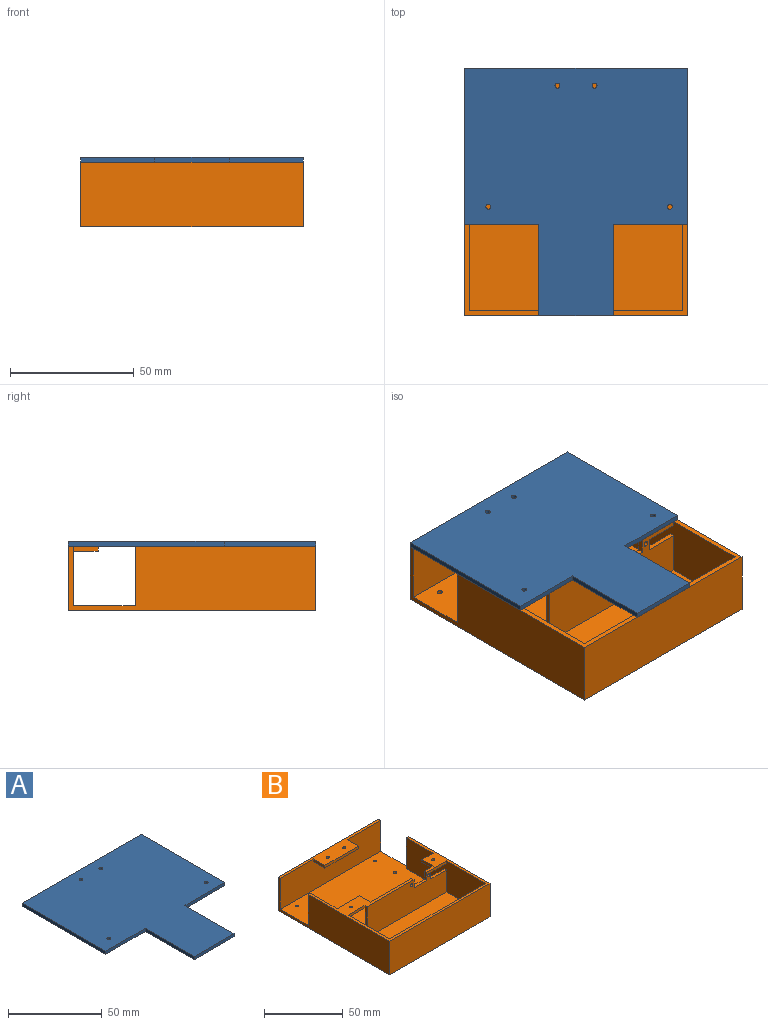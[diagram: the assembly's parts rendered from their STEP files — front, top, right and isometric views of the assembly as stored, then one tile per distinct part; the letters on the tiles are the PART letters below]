
ASSEMBLY  parts=2 mates=1
PART A: 14 faces, bbox 90x100x2 mm
  f0: plane 30x2mm, normal (0,-1,0), area 60mm2, adj f1,f10,f12,f13
  f1: plane 37x2mm, normal (-1,0,0), area 74mm2, adj f0,f2,f12,f13
  f2: plane 30x2mm, normal (0,-1,0), area 60mm2, adj f1,f3,f12,f13
  f3: plane 37x2mm, normal (1,0,0), area 74mm2, adj f2,f4,f12,f13
  f4: plane 30x2mm, normal (0,-1,0), area 60mm2, adj f3,f5,f12,f13
  f5: plane 63x2mm, normal (1,0,0), area 126mm2, adj f4,f6,f12,f13
  f6: plane 90x2mm, normal (0,1,0), area 180mm2, adj f5,f10,f12,f13
  f7: cylinder r=1mm len=2mm, axis (0,0,-1), area 12.6mm2, adj f12,f13
  f8: cylinder r=1mm len=2mm, axis (0,0,-1), area 12.6mm2, adj f12,f13
  f9: cylinder r=1mm len=2mm, axis (0,0,-1), area 12.6mm2, adj f12,f13
  f10: plane 63x2mm, normal (-1,0,0), area 126mm2, adj f0,f6,f12,f13
  f11: cylinder r=1mm len=2mm, axis (0,0,-1), area 12.6mm2, adj f12,f13
  f12: plane 100x90mm, normal (0,0,1), area 6767.4mm2, adj f0,f1,f2,f3,f4,f5,f6,f7
  f13: plane 100x90mm, normal (0,0,-1), area 6767.4mm2, adj f0,f1,f2,f3,f4,f5,f6,f7
PART B: 43 faces, bbox 90x100x26 mm
  f0: plane 71x24mm, normal (0,1,0), area 1528.9mm2, adj f1,f4,f5,f20,f22,f24,f26,f29
  f1: plane 90x73mm, normal (0,0,1), area 877.5mm2, adj f0,f2,f3,f4,f7,f8,f14,f16
  f2: plane 71x24mm, normal (0,-1,0), area 1558.9mm2, adj f1,f4,f5,f20,f24,f36,f37,f38
  f3: plane 71x24mm, normal (1,0,0), area 1684mm2, adj f1,f5,f16,f18,f25,f27,f29
  f4: plane 71x24mm, normal (-1,0,0), area 1646mm2, adj f0,f1,f2,f5,f16,f19,f21,f24
  f5: plane 96x90mm, normal (0,0,1), area 8201.4mm2, adj f0,f2,f3,f4,f8,f10,f11,f12
  f6: plane 90x12mm, normal (0,0,1), area 473.7mm2, adj f8,f9,f14,f17,f30,f31,f32,f33
  f7: plane 90x26mm, normal (0,-1,0), area 2340mm2, adj f1,f8,f14,f15
  f8: plane 100x26mm, normal (1,0,0), area 2000mm2, adj f1,f5,f6,f7,f9,f15,f17,f19
  f9: plane 90x26mm, normal (0,1,0), area 2340mm2, adj f6,f8,f14,f15
  f10: cylinder r=1mm len=2mm, axis (0,0,-1), area 12.6mm2, adj f5,f15
  f11: cylinder r=1mm len=2mm, axis (0,0,-1), area 12.6mm2, adj f5,f15
  f12: cylinder r=1mm len=2mm, axis (0,0,-1), area 12.6mm2, adj f5,f15
  f13: cylinder r=1mm len=2mm, axis (0,0,-1), area 12.6mm2, adj f5,f15
  f14: plane 100x26mm, normal (-1,0,0), area 2000mm2, adj f1,f5,f6,f7,f9,f15,f17,f18
  f15: plane 100x90mm, normal (0,0,-1), area 8987.4mm2, adj f7,f8,f9,f10,f11,f12,f13,f14
  f16: plane 86x24mm, normal (0,1,0), area 2064mm2, adj f1,f3,f4,f5
  f17: plane 90x24mm, normal (0,-1,0), area 2100mm2, adj f5,f6,f8,f14,f30,f31,f35
  f18: plane 24x2mm, normal (0,1,0), area 48mm2, adj f1,f3,f5,f14
  f19: plane 24x2mm, normal (0,1,0), area 48mm2, adj f1,f4,f5,f8
  f20: plane 24x2mm, normal (-1,0,0), area 48mm2, adj f0,f1,f2,f5,f25
  f21: plane 10x2mm, normal (0,1,0), area 20mm2, adj f1,f4,f22,f24
  f22: plane 10x2mm, normal (-1,0,0), area 20mm2, adj f0,f1,f21,f24
  f23: cylinder r=1mm len=2mm, axis (0,0,1), area 12.6mm2, adj f1,f24
  f24: plane 14x12mm, normal (0,0,-1), area 124.9mm2, adj f0,f2,f4,f21,f22,f23,f41
  f25: plane 15x2mm, normal (0,-1,0), area 30mm2, adj f1,f3,f20,f29
  f26: plane 10x2mm, normal (1,0,0), area 20mm2, adj f0,f1,f27,f29
  f27: plane 20x2mm, normal (0,1,0), area 40mm2, adj f1,f3,f26,f29
  f28: cylinder r=1mm len=2mm, axis (0,0,1), area 12.6mm2, adj f1,f29
  f29: plane 20x10mm, normal (0,0,-1), area 196.9mm2, adj f0,f3,f25,f26,f27,f28
  f30: plane 10x2mm, normal (1,0,0), area 20mm2, adj f6,f17,f33,f35
  f31: plane 10x2mm, normal (-1,0,0), area 20mm2, adj f6,f17,f33,f35
  f32: cylinder r=1mm len=2mm, axis (0,0,1), area 12.6mm2, adj f6,f35
  f33: plane 30x2mm, normal (0,-1,0), area 60mm2, adj f6,f30,f31,f35
  f34: cylinder r=1mm len=2mm, axis (0,0,1), area 12.6mm2, adj f6,f35
  f35: plane 30x10mm, normal (0,0,-1), area 293.7mm2, adj f17,f30,f31,f32,f33,f34
  f36: plane 6.2x2mm, normal (1,0,0), area 12.4mm2, adj f0,f1,f2,f38
  f37: plane 6.2x2mm, normal (-1,0,0), area 12.4mm2, adj f0,f1,f2,f38
  f38: plane 11.1x2mm, normal (0,0,1), area 22.2mm2, adj f0,f2,f36,f37
  f39: cylinder r=1mm len=2mm, axis (0,1,0), area 12.6mm2, adj f0,f2
  f40: cylinder r=1mm len=2mm, axis (0,1,0), area 12.6mm2, adj f0,f2
  f41: plane 5x2mm, normal (1,0,0), area 10mm2, adj f0,f2,f24,f42
  f42: plane 14x2mm, normal (0,0,1), area 28mm2, adj f0,f2,f4,f41
PLACE A t=(70.74,40.34,-5.19)mm
PLACE B t=(70.74,21.84,-31.19)mm
MATE fastened B.f6 <-> A.f13  axis (0,0,1) through (70.74,71.84,-5.19)mm
